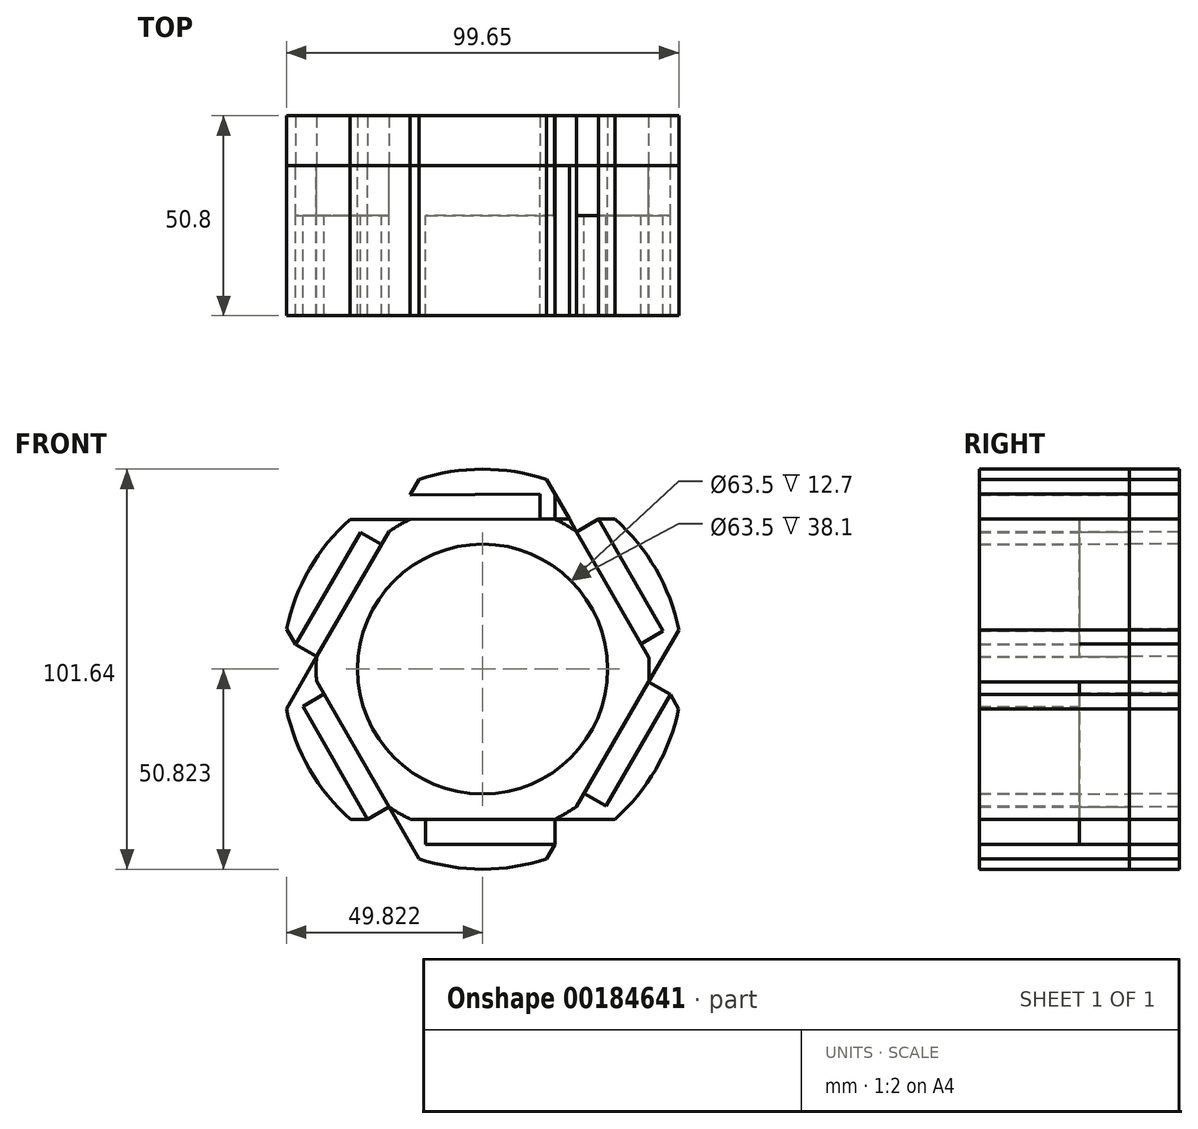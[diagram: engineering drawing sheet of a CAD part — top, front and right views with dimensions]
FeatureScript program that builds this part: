
annotation { "Feature Type Name" : "Feature", "Feature Type Description" : "" }
export const myFeature = defineFeature(function(context is Context, id is Id, definition is map)
    precondition{}
    {
        {
            var Q0;
            Q0=qCreatedBy(makeId("Front.planeOp"),FACE);
            var sketch = newSketch(context, id + "F0", { "sketchPlane" : qUnion([Q0])});
            skCircle(sketch, "E0", {"center": v(-63.43, 38.12) * mm, "radius": 31.75 * mm});
            skLineSegment(sketch, "E1", {"start": v(-35.48, 23) * mm, "end": v(-44.9, 7.28) * mm});
            skLineSegment(sketch, "E2", {"start": v(-79.37, 65.58) * mm, "end": v(-81.92, 69.99) * mm});
            skLineSegment(sketch, "E3", {"start": v(-47.53, 65.6) * mm, "end": v(-45.09, 69.84) * mm});
            skLineSegment(sketch, "E4", {"start": v(-31.68, 38.09) * mm, "end": v(-26.8, 38.08) * mm});
            skLineSegment(sketch, "E5", {"start": v(-47.51, 10.65) * mm, "end": v(-45.06, 6.41) * mm});
            skLineSegment(sketch, "E6", {"start": v(-79.24, 10.6) * mm, "end": v(-81.7, 6.3) * mm});
            skLineSegment(sketch, "E7", {"start": v(-95.18, 38.19) * mm, "end": v(-100.24, 38.2) * mm});
            skLineSegment(sketch, "E8", {"start": v(-81.7, 6.3) * mm, "end": v(-81.7, -6.35) * mm});
            skLineSegment(sketch, "E9", {"start": v(-45.06, 6.41) * mm, "end": v(-45.08, -6.38) * mm});
            skLineSegment(sketch, "E10", {"start": v(-45.06, 6.41) * mm, "end": v(-34, 0.02) * mm});
            skLineSegment(sketch, "E11", {"start": v(-26.8, 38.08) * mm, "end": v(-15.7, 31.68) * mm});
            skLineSegment(sketch, "E12", {"start": v(-26.8, 38.08) * mm, "end": v(-15.7, 44.49) * mm});
            skLineSegment(sketch, "E13", {"start": v(-45.09, 69.84) * mm, "end": v(-34.02, 76.24) * mm});
            skLineSegment(sketch, "E14", {"start": v(-45.09, 69.84) * mm, "end": v(-45.09, 82.63) * mm});
            skLineSegment(sketch, "E15", {"start": v(-81.92, 69.99) * mm, "end": v(-81.9, 82.35) * mm});
            skLineSegment(sketch, "E16", {"start": v(-81.92, 69.99) * mm, "end": v(-92.58, 76.16) * mm});
            skLineSegment(sketch, "E17", {"start": v(-100.24, 38.2) * mm, "end": v(-110.97, 44.4) * mm});
            skLineSegment(sketch, "E18", {"start": v(-100.24, 38.2) * mm, "end": v(-111, 32) * mm});
            skLineSegment(sketch, "E19", {"start": v(-81.7, 6.3) * mm, "end": v(-92.7, -0.02) * mm});
            skLineSegment(sketch, "E20", {"start": v(-81.9, 82.35) * mm, "end": v(-45.09, 82.63) * mm});
            skLineSegment(sketch, "E21", {"start": v(-34.02, 76.24) * mm, "end": v(-15.7, 44.49) * mm});
            skLineSegment(sketch, "E22", {"start": v(-15.7, 31.68) * mm, "end": v(-34, 0.02) * mm});
            skLineSegment(sketch, "E23", {"start": v(-45.08, -6.38) * mm, "end": v(-81.7, -6.35) * mm});
            skLineSegment(sketch, "E24", {"start": v(-92.7, -0.02) * mm, "end": v(-111, 32) * mm});
            skLineSegment(sketch, "E25", {"start": v(-110.97, 44.4) * mm, "end": v(-92.58, 76.16) * mm});
            skPoint(sketch, "E26", {"position": v(-21.25, 41.28) * mm});
            skPoint(sketch, "E27", {"position": v(-39.55, 73.04) * mm});
            skPoint(sketch, "E28", {"position": v(-45.09, 76.24) * mm});
            skPoint(sketch, "E29", {"position": v(-81.9, 76.17) * mm});
            skPoint(sketch, "E30", {"position": v(-87.25, 73.07) * mm});
            skPoint(sketch, "E31", {"position": v(-105.6, 41.3) * mm});
            skPoint(sketch, "E32", {"position": v(-105.62, 35.1) * mm});
            skPoint(sketch, "E33", {"position": v(-87.2, 3.14) * mm});
            skPoint(sketch, "E34", {"position": v(-81.7, -0.02) * mm});
            skPoint(sketch, "E35", {"position": v(-45.07, 0.01) * mm});
            skPoint(sketch, "E36", {"position": v(-39.53, 3.22) * mm});
            skPoint(sketch, "E37", {"position": v(-21.25, 34.88) * mm});
            skLineSegment(sketch, "E38", {"start": v(-21.25, 41.28) * mm, "end": v(-39.55, 73.04) * mm});
            skLineSegment(sketch, "E39", {"start": v(-45.09, 76.24) * mm, "end": v(-81.9, 76.17) * mm});
            skLineSegment(sketch, "E40", {"start": v(-87.25, 73.07) * mm, "end": v(-105.6, 41.3) * mm});
            skLineSegment(sketch, "E41", {"start": v(-105.62, 35.1) * mm, "end": v(-87.2, 3.14) * mm});
            skLineSegment(sketch, "E42", {"start": v(-81.7, -0.02) * mm, "end": v(-45.07, 0.01) * mm});
            skLineSegment(sketch, "E43", {"start": v(-39.53, 3.22) * mm, "end": v(-21.25, 34.88) * mm});
            skArc(sketch, "E44", {"start": v(-97.12, 76.17) * mm, "mid": v(-107.44, 63.54) * mm, "end": v(-113.22, 48.3) * mm});
            skArc(sketch, "E45", {"start": v(-81.9, 76.17) * mm, "mid": v(-84.64, 74.72) * mm, "end": v(-87.25, 73.07) * mm});
            skLineSegment(sketch, "E46", {"start": v(-81.9, 76.17) * mm, "end": v(-81.9, 82.35) * mm});
            skLineSegment(sketch, "E47", {"start": v(-45.09, 76.24) * mm, "end": v(-45.09, 82.63) * mm});
            skArc(sketch, "E48.trimOffspring", {"start": v(-39.55, 73.04) * mm, "mid": v(-42.26, 74.74) * mm, "end": v(-45.09, 76.24) * mm});
            skArc(sketch, "E49.trimOffspring", {"start": v(-21.25, 34.88) * mm, "mid": v(-21.13, 38.08) * mm, "end": v(-21.25, 41.28) * mm});
            skArc(sketch, "E50.trimOffspring", {"start": v(-45.07, 0.01) * mm, "mid": v(-42.24, 1.51) * mm, "end": v(-39.53, 3.22) * mm});
            skArc(sketch, "E51.trimOffspring", {"start": v(-87.2, 3.14) * mm, "mid": v(-84.52, 1.46) * mm, "end": v(-81.7, -0.02) * mm});
            skArc(sketch, "E52.trimOffspring", {"start": v(-105.6, 41.3) * mm, "mid": v(-105.73, 38.2) * mm, "end": v(-105.62, 35.1) * mm});
            skArc(sketch, "E53.trimOffspring", {"start": v(-47.24, 86.3) * mm, "mid": v(-63.43, 88.94) * mm, "end": v(-79.62, 86.3) * mm});
            skArc(sketch, "E54.trimOffspring", {"start": v(-13.6, 48.13) * mm, "mid": v(-19.4, 63.51) * mm, "end": v(-29.81, 76.24) * mm});
            skArc(sketch, "E55.trimOffspring", {"start": v(-29.8, 0.01) * mm, "mid": v(-19.42, 12.7) * mm, "end": v(-13.62, 28.05) * mm});
            skArc(sketch, "E56.trimOffspring", {"start": v(-79.6, -10.06) * mm, "mid": v(-63.4, -12.7) * mm, "end": v(-47.19, -10.03) * mm});
            skArc(sketch, "E57.trimOffspring", {"start": v(-113.25, 28.07) * mm, "mid": v(-107.43, 12.7) * mm, "end": v(-97.01, -0.02) * mm});
            skLineSegment(sketch, "E58", {"start": v(-81.9, 76.17) * mm, "end": v(-97.12, 76.17) * mm});
            skLineSegment(sketch, "E59", {"start": v(-45.09, 76.24) * mm, "end": v(-41.4, 76.24) * mm});
            skLineSegment(sketch, "E60", {"start": v(-87.25, 73.07) * mm, "end": v(-85.46, 76.17) * mm});
            skLineSegment(sketch, "E61", {"start": v(-39.55, 73.04) * mm, "end": v(-47.24, 86.3) * mm});
            skLineSegment(sketch, "E62", {"start": v(-21.25, 41.28) * mm, "end": v(-19.4, 38.08) * mm});
            skLineSegment(sketch, "E63", {"start": v(-39.53, 3.22) * mm, "end": v(-41.38, 0.01) * mm});
            skLineSegment(sketch, "E64", {"start": v(-45.07, 0.01) * mm, "end": v(-29.8, 0.01) * mm});
            skLineSegment(sketch, "E65", {"start": v(-81.7, -0.02) * mm, "end": v(-85.39, -0.02) * mm});
            skLineSegment(sketch, "E66", {"start": v(-87.2, 3.14) * mm, "end": v(-79.6, -10.06) * mm});
            skLineSegment(sketch, "E67", {"start": v(-105.62, 35.1) * mm, "end": v(-107.4, 38.2) * mm});
            skLineSegment(sketch, "E68", {"start": v(-105.6, 41.3) * mm, "end": v(-113.25, 28.07) * mm});
            skLineSegment(sketch, "E69", {"start": v(-21.25, 34.88) * mm, "end": v(-13.6, 48.13) * mm});
            skLineSegment(sketch, "E70.trimOffspring", {"start": v(-34.02, 76.24) * mm, "end": v(-29.81, 76.24) * mm});
            skLineSegment(sketch, "E71.trimOffspring", {"start": v(-81.9, 82.35) * mm, "end": v(-79.62, 86.3) * mm});
            skLineSegment(sketch, "E72.trimOffspring", {"start": v(-110.97, 44.4) * mm, "end": v(-113.22, 48.3) * mm});
            skLineSegment(sketch, "E73.trimOffspring", {"start": v(-92.7, -0.02) * mm, "end": v(-97.01, -0.02) * mm});
            skLineSegment(sketch, "E74.trimOffspring", {"start": v(-45.08, -6.38) * mm, "end": v(-47.19, -10.03) * mm});
            skLineSegment(sketch, "E75.trimOffspring", {"start": v(-15.7, 31.68) * mm, "end": v(-13.62, 28.05) * mm});
            skPoint(sketch, "E76", {"position": v(-101.78, 60.28) * mm});
            skPoint(sketch, "E77", {"position": v(-107.44, 63.54) * mm});
            skPoint(sketch, "E78", {"position": v(-24.86, 60.36) * mm});
            skPoint(sketch, "E79", {"position": v(-19.4, 63.51) * mm});
            skPoint(sketch, "E80", {"position": v(-63.4, -12.7) * mm});
            skPoint(sketch, "E81", {"position": v(-63.4, -6.36) * mm});
            skLineSegment(sketch, "E82", {"start": v(-94.5, 72.86) * mm, "end": v(-89.16, 69.77) * mm});
            skLineSegment(sketch, "E83", {"start": v(-48.9, 76.23) * mm, "end": v(-48.9, 82.6) * mm});
            skLineSegment(sketch, "E84", {"start": v(-23.15, 44.58) * mm, "end": v(-17.6, 47.79) * mm});
            skLineSegment(sketch, "E85", {"start": v(-37.63, 6.52) * mm, "end": v(-32.1, 3.32) * mm});
            skLineSegment(sketch, "E86", {"start": v(-77.9, -6.35) * mm, "end": v(-77.9, 0) * mm});
            skLineSegment(sketch, "E87", {"start": v(-109.1, 28.7) * mm, "end": v(-103.72, 31.8) * mm});
            skSolve(sketch);
        }
        {
            var Q0;
            {var subQ4=sQuery(id+"F0.wireOp",EDGE,"E7");Q0=makeQuery(id+"F0.imprint","IMPRINT",FACE,{"disambiguationData":[TD([[makeQuery(id+"F0.imprint","IMPRINT",EDGE,{"derivedFrom":subQ4}),-1.0]])]});}
            var Q1;
            {var subQ0=sQuery(id+"F0.wireOp",EDGE,"E3");Q1=makeQuery(id+"F0.imprint","IMPRINT",FACE,{"disambiguationData":[TD([[makeQuery(id+"F0.imprint","IMPRINT",EDGE,{"derivedFrom":subQ0}),1.0]])]});}
            var Q2;
            {var subQ0=sQuery(id+"F0.wireOp",EDGE,"E45");Q2=makeQuery(id+"F0.imprint","IMPRINT",FACE,{"disambiguationData":[TD([[makeQuery(id+"F0.imprint","IMPRINT",EDGE,{"derivedFrom":subQ0}),1.0]])]});}
            var Q3;
            {var subQ8=sQuery(id+"F0.wireOp",EDGE,"E3");Q3=makeQuery(id+"F0.imprint","IMPRINT",FACE,{"disambiguationData":[TD([[makeQuery(id+"F0.imprint","IMPRINT",EDGE,{"derivedFrom":subQ8}),-1.0]])]});}
            var Q4;
            {var subQ0=sQuery(id+"F0.wireOp",EDGE,"E14");Q4=makeQuery(id+"F0.imprint","IMPRINT",FACE,{"disambiguationData":[TD([[makeQuery(id+"F0.imprint","IMPRINT",EDGE,{"derivedFrom":subQ0}),-1.0]])]});}
            var Q5;
            {var subQ6=sQuery(id+"F0.wireOp",EDGE,"E1");Q5=makeQuery(id+"F0.imprint","IMPRINT",FACE,{"disambiguationData":[TD([[makeQuery(id+"F0.imprint","IMPRINT",EDGE,{"derivedFrom":subQ6}),1.0]])]});}
            var Q6;
            {var subQ0=sQuery(id+"F0.wireOp",EDGE,"E49.trimOffspring");Q6=makeQuery(id+"F0.imprint","IMPRINT",FACE,{"disambiguationData":[TD([[makeQuery(id+"F0.imprint","IMPRINT",EDGE,{"derivedFrom":subQ0}),1.0]])]});}
            var Q7;
            {var subQ3=sQuery(id+"F0.wireOp",EDGE,"E50.trimOffspring");Q7=makeQuery(id+"F0.imprint","IMPRINT",FACE,{"disambiguationData":[TD([[makeQuery(id+"F0.imprint","IMPRINT",EDGE,{"derivedFrom":subQ3}),1.0]])]});}
            var Q8;
            {var subQ0=sQuery(id+"F0.wireOp",EDGE,"E1");Q8=makeQuery(id+"F0.imprint","IMPRINT",FACE,{"disambiguationData":[TD([[makeQuery(id+"F0.imprint","IMPRINT",EDGE,{"derivedFrom":subQ0}),-1.0]])]});}
            var Q9;
            {var subQ8=sQuery(id+"F0.wireOp",EDGE,"E5");Q9=makeQuery(id+"F0.imprint","IMPRINT",FACE,{"disambiguationData":[TD([[makeQuery(id+"F0.imprint","IMPRINT",EDGE,{"derivedFrom":subQ8}),-1.0]])]});}
            var Q10;
            {var subQ0=sQuery(id+"F0.wireOp",EDGE,"E51.trimOffspring");Q10=makeQuery(id+"F0.imprint","IMPRINT",FACE,{"disambiguationData":[TD([[makeQuery(id+"F0.imprint","IMPRINT",EDGE,{"derivedFrom":subQ0}),1.0]])]});}
            var Q11;
            {var subQ1=sQuery(id+"F0.wireOp",EDGE,"E7");Q11=makeQuery(id+"F0.imprint","IMPRINT",FACE,{"disambiguationData":[TD([[makeQuery(id+"F0.imprint","IMPRINT",EDGE,{"derivedFrom":subQ1}),1.0]])]});}
            var Q12;
            {var subQ3=sQuery(id+"F0.wireOp",EDGE,"E52.trimOffspring");Q12=makeQuery(id+"F0.imprint","IMPRINT",FACE,{"disambiguationData":[TD([[makeQuery(id+"F0.imprint","IMPRINT",EDGE,{"derivedFrom":subQ3}),1.0]])]});}
            var Q13;
            {var subQ3=sQuery(id+"F0.wireOp",EDGE,"E5");Q13=makeQuery(id+"F0.imprint","IMPRINT",FACE,{"disambiguationData":[TD([[makeQuery(id+"F0.imprint","IMPRINT",EDGE,{"derivedFrom":subQ3}),1.0]])]});}
            extrude(context, id + "F1", {"entities" : qUnion([Q0, Q1, Q2, Q3, Q4, Q5, Q6, Q7, Q8, Q9, Q10, Q11, Q12, Q13]), "depth" : 38.1 * mm});
        }
        {
            var Q0;
            Q0=makeQuery(id+"F0.imprint","IMPRINT",FACE,{"disambiguationData":[TD([[makeQuery(id+"F0.imprint","IMPRINT",EDGE,{"derivedFrom":sQuery(id+"F0.wireOp",EDGE,"E25")}),1.0]])]});
            var Q1;
            Q1=makeQuery(id+"F0.imprint","IMPRINT",FACE,{"disambiguationData":[TD([[makeQuery(id+"F0.imprint","IMPRINT",EDGE,{"derivedFrom":sQuery(id+"F0.wireOp",EDGE,"E24")}),1.0]])]});
            var Q2;
            Q2=makeQuery(id+"F0.imprint","IMPRINT",FACE,{"disambiguationData":[TD([[makeQuery(id+"F0.imprint","IMPRINT",EDGE,{"derivedFrom":sQuery(id+"F0.wireOp",EDGE,"E23")}),1.0]])]});
            var Q3;
            Q3=makeQuery(id+"F0.imprint","IMPRINT",FACE,{"disambiguationData":[TD([[makeQuery(id+"F0.imprint","IMPRINT",EDGE,{"derivedFrom":sQuery(id+"F0.wireOp",EDGE,"E22")}),1.0]])]});
            var Q4;
            Q4=makeQuery(id+"F0.imprint","IMPRINT",FACE,{"disambiguationData":[TD([[makeQuery(id+"F0.imprint","IMPRINT",EDGE,{"derivedFrom":sQuery(id+"F0.wireOp",EDGE,"E21")}),1.0]])]});
            var Q5;
            {var subQ0=sQuery(id+"F0.wireOp",EDGE,"E20");Q5=makeQuery(id+"F0.imprint","IMPRINT",FACE,{"disambiguationData":[TD([[makeQuery(id+"F0.imprint","IMPRINT",EDGE,{"derivedFrom":subQ0}),1.0]])]});}
            var Q6;
            {var subQ3=sQuery(id+"F0.wireOp",EDGE,"E60");Q6=makeQuery(id+"F0.imprint","IMPRINT",FACE,{"disambiguationData":[TD([[makeQuery(id+"F0.imprint","IMPRINT",EDGE,{"derivedFrom":subQ3}),1.0]])]});}
            var Q7;
            {var subQ3=sQuery(id+"F0.wireOp",EDGE,"E67");Q7=makeQuery(id+"F0.imprint","IMPRINT",FACE,{"disambiguationData":[TD([[makeQuery(id+"F0.imprint","IMPRINT",EDGE,{"derivedFrom":subQ3}),1.0]])]});}
            var Q8;
            {var subQ3=sQuery(id+"F0.wireOp",EDGE,"E65");Q8=makeQuery(id+"F0.imprint","IMPRINT",FACE,{"disambiguationData":[TD([[makeQuery(id+"F0.imprint","IMPRINT",EDGE,{"derivedFrom":subQ3}),1.0]])]});}
            var Q9;
            {var subQ3=sQuery(id+"F0.wireOp",EDGE,"E63");Q9=makeQuery(id+"F0.imprint","IMPRINT",FACE,{"disambiguationData":[TD([[makeQuery(id+"F0.imprint","IMPRINT",EDGE,{"derivedFrom":subQ3}),1.0]])]});}
            var Q10;
            {var subQ3=sQuery(id+"F0.wireOp",EDGE,"E62");Q10=makeQuery(id+"F0.imprint","IMPRINT",FACE,{"disambiguationData":[TD([[makeQuery(id+"F0.imprint","IMPRINT",EDGE,{"derivedFrom":subQ3}),1.0]])]});}
            var Q11;
            {var subQ0=sQuery(id+"F0.wireOp",EDGE,"E47");Q11=makeQuery(id+"F0.imprint","IMPRINT",FACE,{"disambiguationData":[TD([[makeQuery(id+"F0.imprint","IMPRINT",EDGE,{"derivedFrom":subQ0}),-1.0]])]});}
            var Q12;
            {var subQ0=sQuery(id+"F0.wireOp",EDGE,"E48.trimOffspring");Q12=makeQuery(id+"F0.imprint","IMPRINT",FACE,{"disambiguationData":[TD([[makeQuery(id+"F0.imprint","IMPRINT",EDGE,{"derivedFrom":subQ0}),-1.0]])]});}
            var Q13;
            {var subQ0=sQuery(id+"F0.wireOp",EDGE,"E49.trimOffspring");Q13=makeQuery(id+"F0.imprint","IMPRINT",FACE,{"disambiguationData":[TD([[makeQuery(id+"F0.imprint","IMPRINT",EDGE,{"derivedFrom":subQ0}),-1.0]])]});}
            var Q14;
            {var subQ0=sQuery(id+"F0.wireOp",EDGE,"E50.trimOffspring");Q14=makeQuery(id+"F0.imprint","IMPRINT",FACE,{"disambiguationData":[TD([[makeQuery(id+"F0.imprint","IMPRINT",EDGE,{"derivedFrom":subQ0}),-1.0]])]});}
            var Q15;
            {var subQ0=sQuery(id+"F0.wireOp",EDGE,"E51.trimOffspring");Q15=makeQuery(id+"F0.imprint","IMPRINT",FACE,{"disambiguationData":[TD([[makeQuery(id+"F0.imprint","IMPRINT",EDGE,{"derivedFrom":subQ0}),-1.0]])]});}
            var Q16;
            {var subQ0=sQuery(id+"F0.wireOp",EDGE,"E52.trimOffspring");Q16=makeQuery(id+"F0.imprint","IMPRINT",FACE,{"disambiguationData":[TD([[makeQuery(id+"F0.imprint","IMPRINT",EDGE,{"derivedFrom":subQ0}),-1.0]])]});}
            var Q17;
            {var subQ0=sQuery(id+"F0.wireOp",EDGE,"E45");Q17=makeQuery(id+"F0.imprint","IMPRINT",FACE,{"disambiguationData":[TD([[makeQuery(id+"F0.imprint","IMPRINT",EDGE,{"derivedFrom":subQ0}),-1.0]])]});}
            var Q18;
            {var subQ7=sQuery(id+"F0.wireOp",EDGE,"E83");Q18=makeQuery(id+"F0.imprint","IMPRINT",FACE,{"disambiguationData":[TD([[makeQuery(id+"F0.imprint","IMPRINT",EDGE,{"derivedFrom":subQ7}),-1.0]])]});}
            var Q19;
            {var subQ5=sQuery(id+"F0.wireOp",EDGE,"E82");Q19=makeQuery(id+"F0.imprint","IMPRINT",FACE,{"disambiguationData":[TD([[makeQuery(id+"F0.imprint","IMPRINT",EDGE,{"derivedFrom":subQ5}),1.0]])]});}
            var Q20;
            {var subQ7=sQuery(id+"F0.wireOp",EDGE,"E87");Q20=makeQuery(id+"F0.imprint","IMPRINT",FACE,{"disambiguationData":[TD([[makeQuery(id+"F0.imprint","IMPRINT",EDGE,{"derivedFrom":subQ7}),1.0]])]});}
            var Q21;
            {var subQ0=sQuery(id+"F0.wireOp",EDGE,"E23");var subQ1=sQuery(id+"F0.wireOp",EDGE,"E8");var subQ2=makeQuery(id+"F0.imprint","INTERSECT",VERTEX,{"derivedFrom":[subQ1,subQ0]});Q21=makeQuery(id+"F0.imprint","IMPRINT",FACE,{"disambiguationData":[TD([[makeQuery(id+"F0.imprint","IMPRINT",EDGE,{"disambiguationData":[TD([[subQ2,1.0]])],"derivedFrom":subQ0}),-1.0]])]});}
            var Q22;
            {var subQ5=sQuery(id+"F0.wireOp",EDGE,"E85");Q22=makeQuery(id+"F0.imprint","IMPRINT",FACE,{"disambiguationData":[TD([[makeQuery(id+"F0.imprint","IMPRINT",EDGE,{"derivedFrom":subQ5}),-1.0]])]});}
            var Q23;
            {var subQ5=sQuery(id+"F0.wireOp",EDGE,"E84");Q23=makeQuery(id+"F0.imprint","IMPRINT",FACE,{"disambiguationData":[TD([[makeQuery(id+"F0.imprint","IMPRINT",EDGE,{"derivedFrom":subQ5}),-1.0]])]});}
            extrude(context, id + "F2", {"entities" : qUnion([Q0, Q1, Q2, Q3, Q4, Q5, Q6, Q7, Q8, Q9, Q10, Q11, Q12, Q13, Q14, Q15, Q16, Q17, Q18, Q19, Q20, Q21, Q22, Q23]), "depth" : 38.1 * mm});
        }
        {
            var Q0;
            {var subQ5=sQuery(id+"F0.wireOp",EDGE,"E82");Q0=makeQuery(id+"F0.imprint","IMPRINT",FACE,{"disambiguationData":[TD([[makeQuery(id+"F0.imprint","IMPRINT",EDGE,{"derivedFrom":subQ5}),1.0]])]});}
            var Q1;
            {var subQ5=sQuery(id+"F0.wireOp",EDGE,"E82");Q1=makeQuery(id+"F0.imprint","IMPRINT",FACE,{"disambiguationData":[TD([[makeQuery(id+"F0.imprint","IMPRINT",EDGE,{"derivedFrom":subQ5}),-1.0]])]});}
            var Q2;
            {var subQ0=sQuery(id+"F0.wireOp",EDGE,"E47");var subQ1=sQuery(id+"F0.wireOp",EDGE,"E20");var subQ2=makeQuery(id+"F0.imprint","INTERSECT",VERTEX,{"derivedFrom":[subQ1,subQ0]});Q2=makeQuery(id+"F0.imprint","IMPRINT",FACE,{"disambiguationData":[TD([[makeQuery(id+"F0.imprint","IMPRINT",EDGE,{"disambiguationData":[TD([[subQ2,1.0]])],"derivedFrom":subQ1}),-1.0]])]});}
            var Q3;
            {var subQ0=sQuery(id+"F0.wireOp",EDGE,"E21");var subQ1=sQuery(id+"F0.wireOp",EDGE,"E12");var subQ2=makeQuery(id+"F0.imprint","INTERSECT",VERTEX,{"derivedFrom":[subQ1,subQ0]});Q3=makeQuery(id+"F0.imprint","IMPRINT",FACE,{"disambiguationData":[TD([[makeQuery(id+"F0.imprint","IMPRINT",EDGE,{"disambiguationData":[TD([[subQ2,1.0]])],"derivedFrom":subQ1}),1.0]])]});}
            var Q4;
            {var subQ0=sQuery(id+"F0.wireOp",EDGE,"E24");var subQ1=sQuery(id+"F0.wireOp",EDGE,"E18");var subQ2=makeQuery(id+"F0.imprint","INTERSECT",VERTEX,{"derivedFrom":[subQ1,subQ0]});Q4=makeQuery(id+"F0.imprint","IMPRINT",FACE,{"disambiguationData":[TD([[makeQuery(id+"F0.imprint","IMPRINT",EDGE,{"disambiguationData":[TD([[subQ2,1.0]])],"derivedFrom":subQ1}),1.0]])]});}
            var Q5;
            {var subQ5=sQuery(id+"F0.wireOp",EDGE,"E87");Q5=makeQuery(id+"F0.imprint","IMPRINT",FACE,{"disambiguationData":[TD([[makeQuery(id+"F0.imprint","IMPRINT",EDGE,{"derivedFrom":subQ5}),-1.0]])]});}
            var Q6;
            {var subQ0=sQuery(id+"F0.wireOp",EDGE,"E46");Q6=makeQuery(id+"F0.imprint","IMPRINT",FACE,{"disambiguationData":[TD([[makeQuery(id+"F0.imprint","IMPRINT",EDGE,{"derivedFrom":subQ0}),-1.0]])]});}
            var Q7;
            {var subQ5=sQuery(id+"F0.wireOp",EDGE,"E84");Q7=makeQuery(id+"F0.imprint","IMPRINT",FACE,{"disambiguationData":[TD([[makeQuery(id+"F0.imprint","IMPRINT",EDGE,{"derivedFrom":subQ5}),1.0]])]});}
            var Q8;
            {var subQ5=sQuery(id+"F0.wireOp",EDGE,"E85");Q8=makeQuery(id+"F0.imprint","IMPRINT",FACE,{"disambiguationData":[TD([[makeQuery(id+"F0.imprint","IMPRINT",EDGE,{"derivedFrom":subQ5}),1.0]])]});}
            var Q9;
            {var subQ0=sQuery(id+"F0.wireOp",EDGE,"E23");var subQ5=sQuery(id+"F0.wireOp",EDGE,"E86");var subQ6=makeQuery(id+"F0.imprint","INTERSECT",VERTEX,{"derivedFrom":[subQ0,subQ5]});Q9=makeQuery(id+"F0.imprint","IMPRINT",FACE,{"disambiguationData":[TD([[makeQuery(id+"F0.imprint","IMPRINT",EDGE,{"disambiguationData":[TD([[subQ6,-1.0]])],"derivedFrom":subQ5}),-1.0]])]});}
            extrude(context, id + "F3", {"entities" : qUnion([Q0, Q1, Q2, Q3, Q4, Q5, Q6, Q7, Q8, Q9]), "depth" : 12.7 * mm});
        }
        {
            var Q0;
            {var subQ0=sQuery(id+"F0.wireOp",EDGE,"E21");Q0=makeQuery(id+"F0.imprint","IMPRINT",FACE,{"disambiguationData":[TD([[makeQuery(id+"F0.imprint","IMPRINT",EDGE,{"derivedFrom":subQ0}),1.0]])]});}
            var Q1;
            {var subQ0=sQuery(id+"F0.wireOp",EDGE,"E21");Q1=makeQuery(id+"F0.imprint","IMPRINT",FACE,{"disambiguationData":[TD([[makeQuery(id+"F0.imprint","IMPRINT",EDGE,{"derivedFrom":subQ0}),-1.0]])]});}
            var Q2;
            {var subQ3=sQuery(id+"F0.wireOp",EDGE,"E3");Q2=makeQuery(id+"F0.imprint","IMPRINT",FACE,{"disambiguationData":[TD([[makeQuery(id+"F0.imprint","IMPRINT",EDGE,{"derivedFrom":subQ3}),-1.0]])]});}
            var Q3;
            {var subQ0=sQuery(id+"F0.wireOp",EDGE,"E14");Q3=makeQuery(id+"F0.imprint","IMPRINT",FACE,{"disambiguationData":[TD([[makeQuery(id+"F0.imprint","IMPRINT",EDGE,{"derivedFrom":subQ0}),-1.0]])]});}
            var Q4;
            Q4=makeQuery(id+"F0.imprint","IMPRINT",FACE,{"disambiguationData":[TD([[makeQuery(id+"F0.imprint","IMPRINT",EDGE,{"derivedFrom":sQuery(id+"F0.wireOp",EDGE,"E20")}),-1.0]])]});
            var Q5;
            {var subQ0=sQuery(id+"F0.wireOp",EDGE,"E20");Q5=makeQuery(id+"F0.imprint","IMPRINT",FACE,{"disambiguationData":[TD([[makeQuery(id+"F0.imprint","IMPRINT",EDGE,{"derivedFrom":subQ0}),1.0]])]});}
            var Q6;
            {var subQ0=sQuery(id+"F0.wireOp",EDGE,"E45");Q6=makeQuery(id+"F0.imprint","IMPRINT",FACE,{"disambiguationData":[TD([[makeQuery(id+"F0.imprint","IMPRINT",EDGE,{"derivedFrom":subQ0}),-1.0]])]});}
            var Q7;
            {var subQ0=sQuery(id+"F0.wireOp",EDGE,"E47");Q7=makeQuery(id+"F0.imprint","IMPRINT",FACE,{"disambiguationData":[TD([[makeQuery(id+"F0.imprint","IMPRINT",EDGE,{"derivedFrom":subQ0}),-1.0]])]});}
            var Q8;
            {var subQ0=sQuery(id+"F0.wireOp",EDGE,"E48.trimOffspring");Q8=makeQuery(id+"F0.imprint","IMPRINT",FACE,{"disambiguationData":[TD([[makeQuery(id+"F0.imprint","IMPRINT",EDGE,{"derivedFrom":subQ0}),-1.0]])]});}
            var Q9;
            {var subQ3=sQuery(id+"F0.wireOp",EDGE,"E60");Q9=makeQuery(id+"F0.imprint","IMPRINT",FACE,{"disambiguationData":[TD([[makeQuery(id+"F0.imprint","IMPRINT",EDGE,{"derivedFrom":subQ3}),1.0]])]});}
            var Q10;
            {var subQ0=sQuery(id+"F0.wireOp",EDGE,"E25");Q10=makeQuery(id+"F0.imprint","IMPRINT",FACE,{"disambiguationData":[TD([[makeQuery(id+"F0.imprint","IMPRINT",EDGE,{"derivedFrom":subQ0}),-1.0]])]});}
            var Q11;
            {var subQ0=sQuery(id+"F0.wireOp",EDGE,"E25");Q11=makeQuery(id+"F0.imprint","IMPRINT",FACE,{"disambiguationData":[TD([[makeQuery(id+"F0.imprint","IMPRINT",EDGE,{"derivedFrom":subQ0}),1.0]])]});}
            var Q12;
            {var subQ3=sQuery(id+"F0.wireOp",EDGE,"E52.trimOffspring");Q12=makeQuery(id+"F0.imprint","IMPRINT",FACE,{"disambiguationData":[TD([[makeQuery(id+"F0.imprint","IMPRINT",EDGE,{"derivedFrom":subQ3}),1.0]])]});}
            var Q13;
            {var subQ0=sQuery(id+"F0.wireOp",EDGE,"E52.trimOffspring");Q13=makeQuery(id+"F0.imprint","IMPRINT",FACE,{"disambiguationData":[TD([[makeQuery(id+"F0.imprint","IMPRINT",EDGE,{"derivedFrom":subQ0}),-1.0]])]});}
            var Q14;
            {var subQ3=sQuery(id+"F0.wireOp",EDGE,"E67");Q14=makeQuery(id+"F0.imprint","IMPRINT",FACE,{"disambiguationData":[TD([[makeQuery(id+"F0.imprint","IMPRINT",EDGE,{"derivedFrom":subQ3}),1.0]])]});}
            var Q15;
            {var subQ0=sQuery(id+"F0.wireOp",EDGE,"E24");Q15=makeQuery(id+"F0.imprint","IMPRINT",FACE,{"disambiguationData":[TD([[makeQuery(id+"F0.imprint","IMPRINT",EDGE,{"derivedFrom":subQ0}),-1.0]])]});}
            var Q16;
            {var subQ0=sQuery(id+"F0.wireOp",EDGE,"E24");Q16=makeQuery(id+"F0.imprint","IMPRINT",FACE,{"disambiguationData":[TD([[makeQuery(id+"F0.imprint","IMPRINT",EDGE,{"derivedFrom":subQ0}),1.0]])]});}
            var Q17;
            {var subQ0=sQuery(id+"F0.wireOp",EDGE,"E51.trimOffspring");Q17=makeQuery(id+"F0.imprint","IMPRINT",FACE,{"disambiguationData":[TD([[makeQuery(id+"F0.imprint","IMPRINT",EDGE,{"derivedFrom":subQ0}),-1.0]])]});}
            var Q18;
            {var subQ3=sQuery(id+"F0.wireOp",EDGE,"E65");Q18=makeQuery(id+"F0.imprint","IMPRINT",FACE,{"disambiguationData":[TD([[makeQuery(id+"F0.imprint","IMPRINT",EDGE,{"derivedFrom":subQ3}),1.0]])]});}
            var Q19;
            {var subQ3=sQuery(id+"F0.wireOp",EDGE,"E51.trimOffspring");Q19=makeQuery(id+"F0.imprint","IMPRINT",FACE,{"disambiguationData":[TD([[makeQuery(id+"F0.imprint","IMPRINT",EDGE,{"derivedFrom":subQ3}),1.0]])]});}
            var Q20;
            {var subQ3=sQuery(id+"F0.wireOp",EDGE,"E5");Q20=makeQuery(id+"F0.imprint","IMPRINT",FACE,{"disambiguationData":[TD([[makeQuery(id+"F0.imprint","IMPRINT",EDGE,{"derivedFrom":subQ3}),-1.0]])]});}
            var Q21;
            {var subQ0=sQuery(id+"F0.wireOp",EDGE,"E23");Q21=makeQuery(id+"F0.imprint","IMPRINT",FACE,{"disambiguationData":[TD([[makeQuery(id+"F0.imprint","IMPRINT",EDGE,{"derivedFrom":subQ0}),-1.0]])]});}
            var Q22;
            {var subQ0=sQuery(id+"F0.wireOp",EDGE,"E23");Q22=makeQuery(id+"F0.imprint","IMPRINT",FACE,{"disambiguationData":[TD([[makeQuery(id+"F0.imprint","IMPRINT",EDGE,{"derivedFrom":subQ0}),1.0]])]});}
            var Q23;
            {var subQ0=sQuery(id+"F0.wireOp",EDGE,"E1");Q23=makeQuery(id+"F0.imprint","IMPRINT",FACE,{"disambiguationData":[TD([[makeQuery(id+"F0.imprint","IMPRINT",EDGE,{"derivedFrom":subQ0}),-1.0]])]});}
            var Q24;
            {var subQ1=sQuery(id+"F0.wireOp",EDGE,"E1");Q24=makeQuery(id+"F0.imprint","IMPRINT",FACE,{"disambiguationData":[TD([[makeQuery(id+"F0.imprint","IMPRINT",EDGE,{"derivedFrom":subQ1}),1.0]])]});}
            var Q25;
            {var subQ3=sQuery(id+"F0.wireOp",EDGE,"E50.trimOffspring");Q25=makeQuery(id+"F0.imprint","IMPRINT",FACE,{"disambiguationData":[TD([[makeQuery(id+"F0.imprint","IMPRINT",EDGE,{"derivedFrom":subQ3}),1.0]])]});}
            var Q26;
            {var subQ0=sQuery(id+"F0.wireOp",EDGE,"E50.trimOffspring");Q26=makeQuery(id+"F0.imprint","IMPRINT",FACE,{"disambiguationData":[TD([[makeQuery(id+"F0.imprint","IMPRINT",EDGE,{"derivedFrom":subQ0}),-1.0]])]});}
            var Q27;
            {var subQ3=sQuery(id+"F0.wireOp",EDGE,"E63");Q27=makeQuery(id+"F0.imprint","IMPRINT",FACE,{"disambiguationData":[TD([[makeQuery(id+"F0.imprint","IMPRINT",EDGE,{"derivedFrom":subQ3}),1.0]])]});}
            var Q28;
            {var subQ0=sQuery(id+"F0.wireOp",EDGE,"E22");Q28=makeQuery(id+"F0.imprint","IMPRINT",FACE,{"disambiguationData":[TD([[makeQuery(id+"F0.imprint","IMPRINT",EDGE,{"derivedFrom":subQ0}),-1.0]])]});}
            var Q29;
            {var subQ0=sQuery(id+"F0.wireOp",EDGE,"E22");Q29=makeQuery(id+"F0.imprint","IMPRINT",FACE,{"disambiguationData":[TD([[makeQuery(id+"F0.imprint","IMPRINT",EDGE,{"derivedFrom":subQ0}),1.0]])]});}
            var Q30;
            {var subQ3=sQuery(id+"F0.wireOp",EDGE,"E49.trimOffspring");Q30=makeQuery(id+"F0.imprint","IMPRINT",FACE,{"disambiguationData":[TD([[makeQuery(id+"F0.imprint","IMPRINT",EDGE,{"derivedFrom":subQ3}),1.0]])]});}
            var Q31;
            {var subQ0=sQuery(id+"F0.wireOp",EDGE,"E49.trimOffspring");Q31=makeQuery(id+"F0.imprint","IMPRINT",FACE,{"disambiguationData":[TD([[makeQuery(id+"F0.imprint","IMPRINT",EDGE,{"derivedFrom":subQ0}),-1.0]])]});}
            var Q32;
            {var subQ3=sQuery(id+"F0.wireOp",EDGE,"E62");Q32=makeQuery(id+"F0.imprint","IMPRINT",FACE,{"disambiguationData":[TD([[makeQuery(id+"F0.imprint","IMPRINT",EDGE,{"derivedFrom":subQ3}),1.0]])]});}
            var Q33;
            {var subQ0=sQuery(id+"F0.wireOp",EDGE,"E3");Q33=makeQuery(id+"F0.imprint","IMPRINT",FACE,{"disambiguationData":[TD([[makeQuery(id+"F0.imprint","IMPRINT",EDGE,{"derivedFrom":subQ0}),1.0]])]});}
            var Q34;
            {var subQ4=sQuery(id+"F0.wireOp",EDGE,"E7");Q34=makeQuery(id+"F0.imprint","IMPRINT",FACE,{"disambiguationData":[TD([[makeQuery(id+"F0.imprint","IMPRINT",EDGE,{"derivedFrom":subQ4}),-1.0]])]});}
            var Q35;
            {var subQ1=sQuery(id+"F0.wireOp",EDGE,"E7");Q35=makeQuery(id+"F0.imprint","IMPRINT",FACE,{"disambiguationData":[TD([[makeQuery(id+"F0.imprint","IMPRINT",EDGE,{"derivedFrom":subQ1}),1.0]])]});}
            var Q36;
            {var subQ0=sQuery(id+"F0.wireOp",EDGE,"E45");Q36=makeQuery(id+"F0.imprint","IMPRINT",FACE,{"disambiguationData":[TD([[makeQuery(id+"F0.imprint","IMPRINT",EDGE,{"derivedFrom":subQ0}),1.0]])]});}
            var Q37;
            {var subQ7=sQuery(id+"F0.wireOp",EDGE,"E87");Q37=makeQuery(id+"F0.imprint","IMPRINT",FACE,{"disambiguationData":[TD([[makeQuery(id+"F0.imprint","IMPRINT",EDGE,{"derivedFrom":subQ7}),1.0]])]});}
            var Q38;
            {var subQ3=sQuery(id+"F0.wireOp",EDGE,"E5");Q38=makeQuery(id+"F0.imprint","IMPRINT",FACE,{"disambiguationData":[TD([[makeQuery(id+"F0.imprint","IMPRINT",EDGE,{"derivedFrom":subQ3}),1.0]])]});}
            var Q39;
            {var subQ0=sQuery(id+"F0.wireOp",EDGE,"E46");Q39=makeQuery(id+"F0.imprint","IMPRINT",FACE,{"disambiguationData":[TD([[makeQuery(id+"F0.imprint","IMPRINT",EDGE,{"derivedFrom":subQ0}),-1.0]])]});}
            var Q40;
            {var subQ7=sQuery(id+"F0.wireOp",EDGE,"E83");Q40=makeQuery(id+"F0.imprint","IMPRINT",FACE,{"disambiguationData":[TD([[makeQuery(id+"F0.imprint","IMPRINT",EDGE,{"derivedFrom":subQ7}),-1.0]])]});}
            var Q41;
            {var subQ5=sQuery(id+"F0.wireOp",EDGE,"E87");Q41=makeQuery(id+"F0.imprint","IMPRINT",FACE,{"disambiguationData":[TD([[makeQuery(id+"F0.imprint","IMPRINT",EDGE,{"derivedFrom":subQ5}),-1.0]])]});}
            var Q42;
            {var subQ5=sQuery(id+"F0.wireOp",EDGE,"E84");Q42=makeQuery(id+"F0.imprint","IMPRINT",FACE,{"disambiguationData":[TD([[makeQuery(id+"F0.imprint","IMPRINT",EDGE,{"derivedFrom":subQ5}),1.0]])]});}
            var Q43;
            {var subQ5=sQuery(id+"F0.wireOp",EDGE,"E84");Q43=makeQuery(id+"F0.imprint","IMPRINT",FACE,{"disambiguationData":[TD([[makeQuery(id+"F0.imprint","IMPRINT",EDGE,{"derivedFrom":subQ5}),-1.0]])]});}
            extrude(context, id + "F4", {"entities" : qUnion([Q0, Q1, Q2, Q3, Q4, Q5, Q6, Q7, Q8, Q9, Q10, Q11, Q12, Q13, Q14, Q15, Q16, Q17, Q18, Q19, Q20, Q21, Q22, Q23, Q24, Q25, Q26, Q27, Q28, Q29, Q30, Q31, Q32, Q33, Q34, Q35, Q36, Q37, Q38, Q39, Q40, Q41, Q42, Q43]), "oppositeDirection" : true, "depth" : 12.7 * mm});
        }
        {
            var Q0;
            Q0=makeQuery(id+"F2.opExtrude","SWEPT_BODY",BODY,{"disambiguationData":[OSD([sQuery(id+"F0.wireOp",EDGE,"E12"),sQuery(id+"F0.wireOp",EDGE,"E49.trimOffspring"),sQuery(id+"F0.wireOp",EDGE,"E69")])]});
            var Q1;
            Q1=makeQuery(id+"F3.opExtrude","SWEPT_BODY",BODY,{"disambiguationData":[OSD([sQuery(id+"F0.wireOp",EDGE,"E12"),sQuery(id+"F0.wireOp",EDGE,"E13"),sQuery(id+"F0.wireOp",EDGE,"E21"),sQuery(id+"F0.wireOp",EDGE,"E38")])]});
            var Q2;
            Q2=makeQuery(id+"F3.opExtrude","SWEPT_BODY",BODY,{"disambiguationData":[OSD([sQuery(id+"F0.wireOp",EDGE,"E10"),sQuery(id+"F0.wireOp",EDGE,"E11"),sQuery(id+"F0.wireOp",EDGE,"E22"),sQuery(id+"F0.wireOp",EDGE,"E43")])]});
            var Q3;
            Q3=makeQuery(id+"F2.opExtrude","SWEPT_BODY",BODY,{"disambiguationData":[OSD([sQuery(id+"F0.wireOp",EDGE,"E10"),sQuery(id+"F0.wireOp",EDGE,"E50.trimOffspring"),sQuery(id+"F0.wireOp",EDGE,"E64")])]});
            var Q4;
            Q4=makeQuery(id+"F3.opExtrude","SWEPT_BODY",BODY,{"disambiguationData":[OSD([sQuery(id+"F0.wireOp",EDGE,"E8"),sQuery(id+"F0.wireOp",EDGE,"E9"),sQuery(id+"F0.wireOp",EDGE,"E23"),sQuery(id+"F0.wireOp",EDGE,"E42")])]});
            var Q5;
            Q5=makeQuery(id+"F2.opExtrude","SWEPT_BODY",BODY,{"disambiguationData":[OSD([sQuery(id+"F0.wireOp",EDGE,"E8"),sQuery(id+"F0.wireOp",EDGE,"E51.trimOffspring"),sQuery(id+"F0.wireOp",EDGE,"E66")])]});
            var Q6;
            Q6=makeQuery(id+"F3.opExtrude","SWEPT_BODY",BODY,{"disambiguationData":[OSD([sQuery(id+"F0.wireOp",EDGE,"E18"),sQuery(id+"F0.wireOp",EDGE,"E19"),sQuery(id+"F0.wireOp",EDGE,"E24"),sQuery(id+"F0.wireOp",EDGE,"E41")])]});
            var Q7;
            Q7=makeQuery(id+"F3.opExtrude","SWEPT_BODY",BODY,{"disambiguationData":[OSD([sQuery(id+"F0.wireOp",EDGE,"E16"),sQuery(id+"F0.wireOp",EDGE,"E17"),sQuery(id+"F0.wireOp",EDGE,"E25"),sQuery(id+"F0.wireOp",EDGE,"E40")])]});
            var Q8;
            Q8=makeQuery(id+"F2.opExtrude","SWEPT_BODY",BODY,{"disambiguationData":[OSD([sQuery(id+"F0.wireOp",EDGE,"E16"),sQuery(id+"F0.wireOp",EDGE,"E45"),sQuery(id+"F0.wireOp",EDGE,"E58")])]});
            var Q9;
            Q9=makeQuery(id+"F3.opExtrude","SWEPT_BODY",BODY,{"disambiguationData":[OSD([sQuery(id+"F0.wireOp",EDGE,"E20"),sQuery(id+"F0.wireOp",EDGE,"E39"),sQuery(id+"F0.wireOp",EDGE,"E46"),sQuery(id+"F0.wireOp",EDGE,"E47")])]});
            var Q10;
            Q10=makeQuery(id+"F2.opExtrude","SWEPT_BODY",BODY,{"disambiguationData":[OSD([sQuery(id+"F0.wireOp",EDGE,"E47"),sQuery(id+"F0.wireOp",EDGE,"E48.trimOffspring"),sQuery(id+"F0.wireOp",EDGE,"E61")])]});
            var Q11;
            Q11=makeQuery(id+"F2.opExtrude","SWEPT_BODY",BODY,{"disambiguationData":[OSD([sQuery(id+"F0.wireOp",EDGE,"E18"),sQuery(id+"F0.wireOp",EDGE,"E52.trimOffspring"),sQuery(id+"F0.wireOp",EDGE,"E68")])]});
            booleanBodies(context, id + "F5", {"operationType" : BooleanOperationType.UNION, "tools" : qUnion([Q0, Q1, Q2, Q3, Q4, Q5, Q6, Q7, Q8, Q9, Q10, Q11])});
        }
    });
